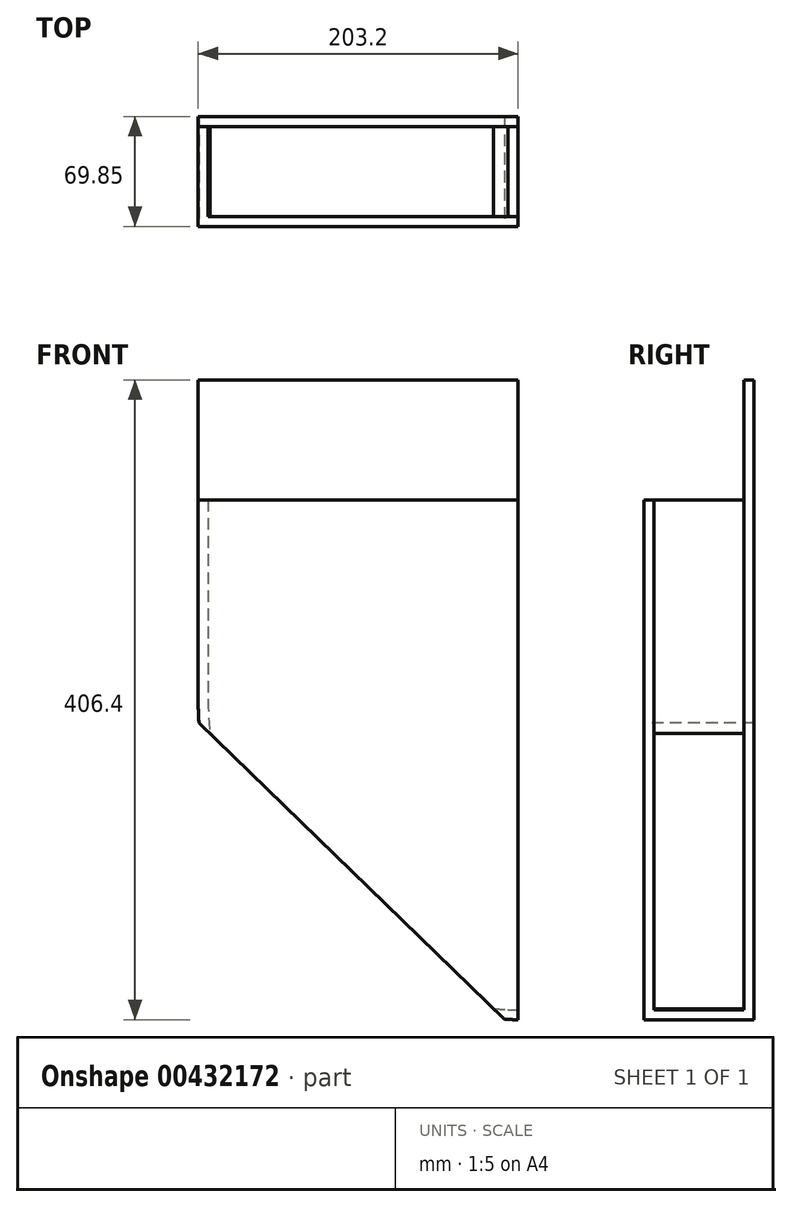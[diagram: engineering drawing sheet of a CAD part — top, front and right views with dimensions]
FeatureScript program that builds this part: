
annotation { "Feature Type Name" : "Feature", "Feature Type Description" : "" }
export const myFeature = defineFeature(function(context is Context, id is Id, definition is map)
    precondition{}
    {
        {
            var Q0;
            Q0=qCreatedBy(makeId("Front.planeOp"),FACE);
            var sketch = newSketch(context, id + "F0", { "sketchPlane" : qUnion([Q0])});
            skLineSegment(sketch, "E0.bottom", {"start": v(-115.03, 217.9) * mm, "end": v(88.17, 217.9) * mm});
            skLineSegment(sketch, "E0.top", {"start": v(-115.03, -188.5) * mm, "end": v(88.17, -188.5) * mm});
            skLineSegment(sketch, "E0.left", {"start": v(-115.03, 217.9) * mm, "end": v(-115.03, -188.5) * mm});
            skLineSegment(sketch, "E0.right", {"start": v(88.17, 217.9) * mm, "end": v(88.17, -188.5) * mm});
            skSolve(sketch);
        }
        {
            var Q0;
            Q0=makeQuery(id+"F0.imprint","IMPRINT",FACE,{"disambiguationData":[TD([[makeQuery(id+"F0.imprint","IMPRINT",EDGE,{"derivedFrom":sQuery(id+"F0.wireOp",EDGE,"E0.bottom")}),-1.0]])]});
            extrude(context, id + "F1", {"entities" : qUnion([Q0]), "depth" : 69.85 * mm});
        }
        {
            var Q0;
            Q0=makeQuery(id+"F1.opExtrude","SWEPT_EDGE",EDGE,{"disambiguationData":[OSD([sQuery(id+"F0.wireOp",EDGE,"E0.top"),sQuery(id+"F0.wireOp",EDGE,"E0.left")])]});
            fillet(context, id + "F2", {"entities" : qUnion([Q0]), "radius" : 203.2 * mm, "tangentPropagation" : true, "allowEdgeOverflow" : false});
        }
        {
            var Q0;
            Q0=makeQuery(id+"F1.opExtrude","SWEPT_FACE",FACE,{"disambiguationData":[OSD([sQuery(id+"F0.wireOp",EDGE,"E0.bottom")])]});
            shell(context, id + "F3", {"entities" : qUnion([Q0]), "thickness" : 6.35 * mm});
        }
        {
            var Q0;
            Q0=makeQuery(id+"F1.opExtrude","SWEPT_FACE",FACE,{"disambiguationData":[OSD([sQuery(id+"F0.wireOp",EDGE,"E0.right")])]});
            var sketch = newSketch(context, id + "F4", { "sketchPlane" : qUnion([Q0])});
            skLineSegment(sketch, "E1.bottom", {"start": v(-63.5, 217.9) * mm, "end": v(-6.35, 217.9) * mm});
            skLineSegment(sketch, "E1.top", {"start": v(-63.5, -182.15) * mm, "end": v(-6.35, -182.15) * mm});
            skLineSegment(sketch, "E1.left", {"start": v(-63.5, 217.9) * mm, "end": v(-63.5, -182.15) * mm});
            skLineSegment(sketch, "E1.right", {"start": v(-6.35, 217.9) * mm, "end": v(-6.35, -182.15) * mm});
            skSolve(sketch);
        }
        {
            var Q0;
            Q0=makeQuery(id+"F4.imprint","IMPRINT",FACE,{"disambiguationData":[TD([[makeQuery(id+"F4.imprint","IMPRINT",EDGE,{"derivedFrom":sQuery(id+"F4.wireOp",EDGE,"E1.bottom")}),-1.0]])]});
            extrude(context, id + "F5", {"entities" : qUnion([Q0]), "operationType" : NewBodyOperationType.REMOVE, "oppositeDirection" : true, "depth" : 6.35 * mm});
        }
        {
            var Q0;
            Q0=makeQuery(id+"F1.opExtrude","SWEPT_FACE",FACE,{"disambiguationData":[OSD([sQuery(id+"F0.wireOp",EDGE,"E0.left")])]});
            var sketch = newSketch(context, id + "F6", { "sketchPlane" : qUnion([Q0])});
            skLineSegment(sketch, "E2.bottom", {"start": v(6.35, 217.9) * mm, "end": v(69.85, 217.9) * mm});
            skLineSegment(sketch, "E2.top", {"start": v(6.35, 141.7) * mm, "end": v(69.85, 141.7) * mm});
            skLineSegment(sketch, "E2.left", {"start": v(6.35, 217.9) * mm, "end": v(6.35, 141.7) * mm});
            skLineSegment(sketch, "E2.right", {"start": v(69.85, 217.9) * mm, "end": v(69.85, 141.7) * mm});
            skSolve(sketch);
        }
        {
            var Q0;
            Q0=makeQuery(id+"F6.imprint","IMPRINT",FACE,{"disambiguationData":[TD([[makeQuery(id+"F6.imprint","IMPRINT",EDGE,{"derivedFrom":sQuery(id+"F6.wireOp",EDGE,"E2.bottom")}),1.0]])]});
            extrude(context, id + "F7", {"entities" : qUnion([Q0]), "operationType" : NewBodyOperationType.REMOVE, "oppositeDirection" : true, "depth" : 203.2 * mm});
        }
        {
            var Q0;
            Q0=makeQuery(id+"F1.opExtrude","CAP_FACE",FACE,{"disambiguationData":[OSD([sQuery(id+"F0.wireOp",EDGE,"E0.bottom"),sQuery(id+"F0.wireOp",EDGE,"E0.top"),sQuery(id+"F0.wireOp",EDGE,"E0.left"),sQuery(id+"F0.wireOp",EDGE,"E0.right")])],"isStart":false});
            var sketch = newSketch(context, id + "F8", { "sketchPlane" : qUnion([Q0])});
            skLineSegment(sketch, "E3", {"start": v(-114.5, 0) * mm, "end": v(79.37, -188.3) * mm});
            skSolve(sketch);
        }
        {
            var Q0;
            {var subQ0=sQuery(id+"F8.wireOp",EDGE,"E3");Q0=makeQuery(id+"F8.imprint","IMPRINT",FACE,{"disambiguationData":[TD([[makeQuery(id+"F8.imprint","IMPRINT",EDGE,{"derivedFrom":subQ0}),-1.0]])]});}
            extrude(context, id + "F9", {"entities" : qUnion([Q0]), "operationType" : NewBodyOperationType.REMOVE, "oppositeDirection" : true, "depth" : 76.2 * mm});
        }
    });
